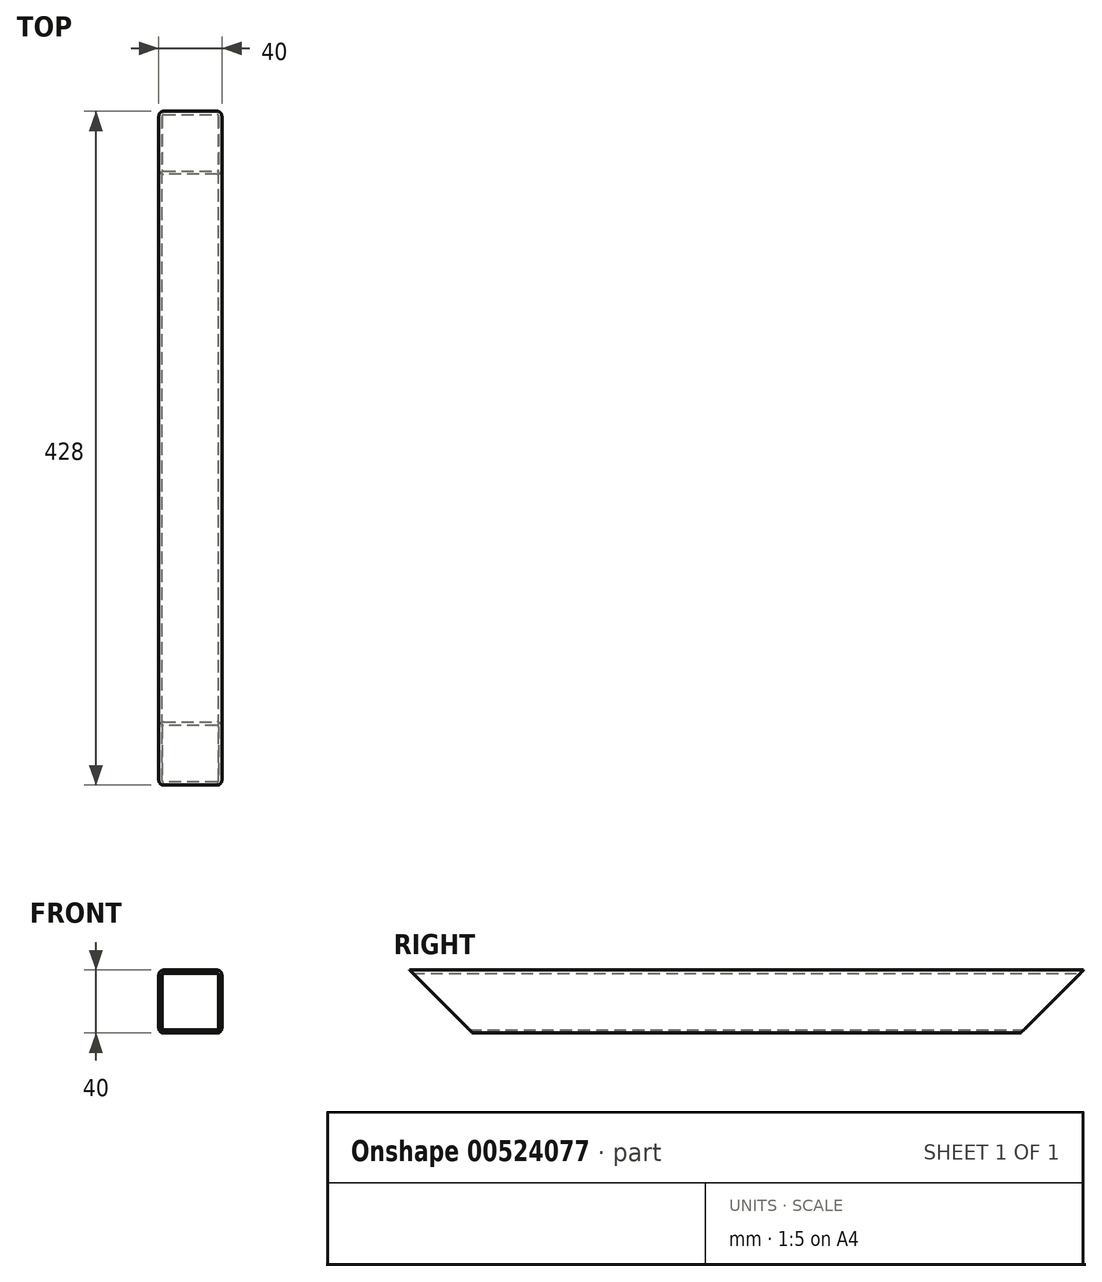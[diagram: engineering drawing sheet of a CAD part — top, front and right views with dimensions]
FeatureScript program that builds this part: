
annotation { "Feature Type Name" : "Feature", "Feature Type Description" : "" }
export const myFeature = defineFeature(function(context is Context, id is Id, definition is map)
    precondition{}
    {
        {
            assignVariable(context, id + "F0", {"name" : "R", "anyValue" : 3});
        }
        {
            assignVariable(context, id + "F1", {"name" : "W", "anyValue" : 2});
        }
        {
            var Q0;
            Q0=qCreatedBy(makeId("Front.planeOp"),FACE);
            var sketch = newSketch(context, id + "F2", { "sketchPlane" : qUnion([Q0])});
            skLineSegment(sketch, "E0.bottom", {"start": v(-20, 20) * mm, "end": v(20, 20) * mm});
            skLineSegment(sketch, "E0.top", {"start": v(-20, -20) * mm, "end": v(20, -20) * mm});
            skLineSegment(sketch, "E0.left", {"start": v(-20, 20) * mm, "end": v(-20, -20) * mm});
            skLineSegment(sketch, "E0.right", {"start": v(20, 20) * mm, "end": v(20, -20) * mm});
            skSolve(sketch);
        }
        {
            var Q0;
            Q0=qSketchRegion(id+"F2",true);
            extrude(context, id + "F3", {"entities" : qUnion([Q0]), "endBound" : BoundingType.SYMMETRIC, "depth" : 428 * mm, "offsetDistance" : 25 * mm});
        }
        {
            var Q0;
            Q0=makeQuery(id+"F3.opExtrude","SWEPT_EDGE",EDGE,{"disambiguationData":[OSD([sQuery(id+"F2.wireOp",EDGE,"E0.bottom"),sQuery(id+"F2.wireOp",EDGE,"E0.right")])]});
            var Q1;
            Q1=makeQuery(id+"F3.opExtrude","SWEPT_EDGE",EDGE,{"disambiguationData":[OSD([sQuery(id+"F2.wireOp",EDGE,"E0.bottom"),sQuery(id+"F2.wireOp",EDGE,"E0.left")])]});
            var Q2;
            Q2=makeQuery(id+"F3.opExtrude","SWEPT_EDGE",EDGE,{"disambiguationData":[OSD([sQuery(id+"F2.wireOp",EDGE,"E0.top"),sQuery(id+"F2.wireOp",EDGE,"E0.right")])]});
            var Q3;
            Q3=makeQuery(id+"F3.opExtrude","SWEPT_EDGE",EDGE,{"disambiguationData":[OSD([sQuery(id+"F2.wireOp",EDGE,"E0.top"),sQuery(id+"F2.wireOp",EDGE,"E0.left")])]});
            fillet(context, id + "F4", {"entities" : qUnion([Q0, Q1, Q2, Q3]), "radius" : (getVariable(context, 'R')) * mm, "tangentPropagation" : true, "allowEdgeOverflow" : false});
        }
        {
            var Q0;
            Q0=makeQuery(id+"F3.opExtrude","CAP_FACE",FACE,{"disambiguationData":[OSD([sQuery(id+"F2.wireOp",EDGE,"E0.bottom"),sQuery(id+"F2.wireOp",EDGE,"E0.top"),sQuery(id+"F2.wireOp",EDGE,"E0.left"),sQuery(id+"F2.wireOp",EDGE,"E0.right")])],"isStart":false});
            var Q1;
            Q1=makeQuery(id+"F3.opExtrude","CAP_FACE",FACE,{"disambiguationData":[OSD([sQuery(id+"F2.wireOp",EDGE,"E0.bottom"),sQuery(id+"F2.wireOp",EDGE,"E0.top"),sQuery(id+"F2.wireOp",EDGE,"E0.left"),sQuery(id+"F2.wireOp",EDGE,"E0.right")])],"isStart":true});
            shell(context, id + "F5", {"entities" : qUnion([Q0, Q1]), "thickness" : (getVariable(context, 'W')) * mm});
        }
        {
            var Q0;
            Q0=makeQuery(id+"F3.opExtrude","SWEPT_FACE",FACE,{"disambiguationData":[OSD([sQuery(id+"F2.wireOp",EDGE,"E0.left")])]});
            var sketch = newSketch(context, id + "F6", { "sketchPlane" : qUnion([Q0])});
            skLineSegment(sketch, "E1", {"start": v(-214, -20) * mm, "end": v(-174, -20) * mm});
            skLineSegment(sketch, "E2", {"start": v(-174, -20) * mm, "end": v(-214, 20) * mm});
            skLineSegment(sketch, "E3", {"start": v(-214, 20) * mm, "end": v(-214, -20) * mm});
            skSolve(sketch);
        }
        {
            var Q0;
            Q0=qSketchRegion(id+"F6",true);
            extrude(context, id + "F7", {"entities" : qUnion([Q0]), "operationType" : NewBodyOperationType.REMOVE, "endBound" : BoundingType.THROUGH_ALL, "oppositeDirection" : true, "depth" : 25 * mm, "offsetDistance" : 25 * mm});
        }
        {
            var Q0;
            Q0=makeQuery(id+"F3.opExtrude","SWEPT_FACE",FACE,{"disambiguationData":[OSD([sQuery(id+"F2.wireOp",EDGE,"E0.right")])]});
            var sketch = newSketch(context, id + "F8", { "sketchPlane" : qUnion([Q0])});
            skLineSegment(sketch, "E4.0", {"start": v(174, -20) * mm, "end": v(-214, -20) * mm, "construction": true});
            skLineSegment(sketch, "E4.1", {"start": v(-214, 20) * mm, "end": v(214, 20) * mm, "construction": true});
            skLineSegment(sketch, "E5", {"start": v(-174, -20) * mm, "end": v(-214, 20) * mm});
            skLineSegment(sketch, "E6", {"start": v(-214, -20) * mm, "end": v(-174, -20) * mm});
            skLineSegment(sketch, "E7", {"start": v(-214, 20) * mm, "end": v(-214, -20) * mm});
            skSolve(sketch);
        }
        {
            var Q0;
            Q0 = qSketchRegion(id + "F8", true);
            extrude(context, id + "F9", {"entities" : qUnion([Q0]), "operationType" : NewBodyOperationType.REMOVE, "endBound" : BoundingType.THROUGH_ALL, "oppositeDirection" : true, "depth" : 25 * mm, "offsetDistance" : 25 * mm});
        }
    });
